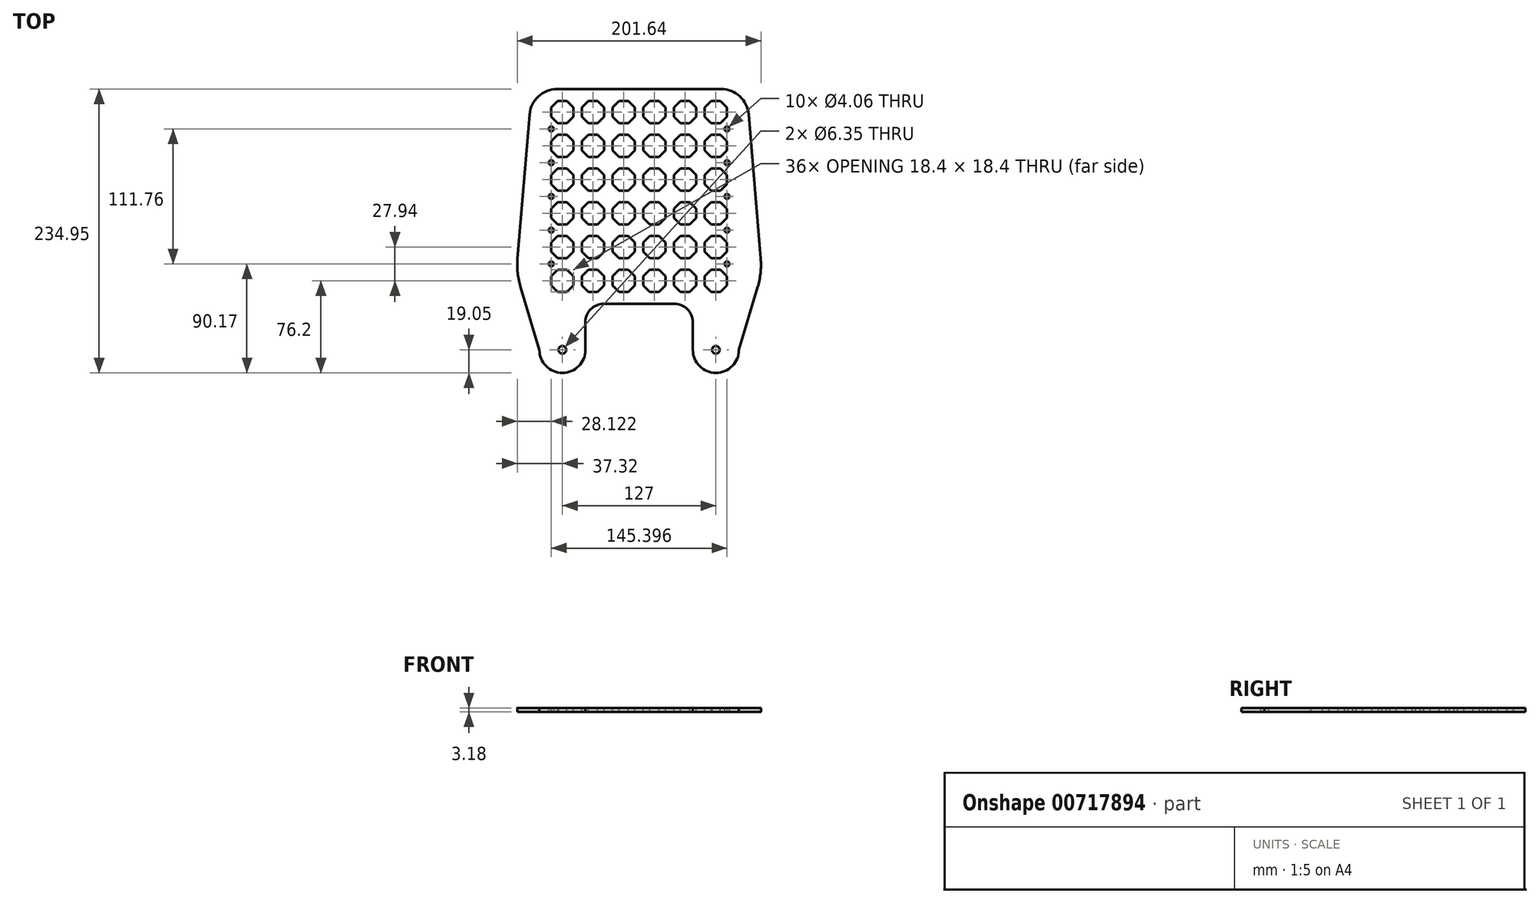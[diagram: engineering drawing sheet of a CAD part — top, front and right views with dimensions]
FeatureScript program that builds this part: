
annotation { "Feature Type Name" : "Feature", "Feature Type Description" : "" }
export const myFeature = defineFeature(function(context is Context, id is Id, definition is map)
    precondition{}
    {
        {
            var Q0;
            Q0=qCreatedBy(makeId("Top.planeOp"),FACE);
            var sketch = newSketch(context, id + "F0", { "sketchPlane" : qUnion([Q0])});
            skLineSegment(sketch, "E0.bottom", {"start": v(-67.87, 152.4) * mm, "end": v(67.87, 152.4) * mm});
            skPoint(sketch, "E0.middle", {"position": v(0, 0) * mm});
            skLineSegment(sketch, "E1", {"start": v(-101.6, 0) * mm, "end": v(101.6, 0) * mm});
            skLineSegment(sketch, "E2", {"start": v(0, 152.4) * mm, "end": v(0, 0) * mm, "construction": true});
            skLineSegment(sketch, "E3", {"start": v(-90.65, 131.44) * mm, "end": v(-100.6, 12) * mm});
            skLineSegment(sketch, "E4", {"start": v(90.65, 131.44) * mm, "end": v(100.6, 12) * mm});
            skLineSegment(sketch, "E5.top", {"start": v(-29.21, -25.4) * mm, "end": v(29.2, -25.4) * mm});
            skLineSegment(sketch, "E5.left", {"start": v(-101.6, 0) * mm, "end": v(-101.6, -25.4) * mm});
            skLineSegment(sketch, "E5.right", {"start": v(101.6, 0) * mm, "end": v(101.6, -25.4) * mm});
            skLineSegment(sketch, "E6.bottom", {"start": v(-82.55, -25.4) * mm, "end": v(-44.45, -25.4) * mm});
            skLineSegment(sketch, "E6.top", {"start": v(-82.55, -63.5) * mm, "end": v(-44.45, -63.5) * mm});
            skLineSegment(sketch, "E6.left", {"start": v(-82.55, -25.4) * mm, "end": v(-82.55, -63.5) * mm});
            skLineSegment(sketch, "E6.right", {"start": v(-44.45, -40.64) * mm, "end": v(-44.45, -63.5) * mm});
            skLineSegment(sketch, "E7.bottom", {"start": v(44.45, -25.4) * mm, "end": v(82.55, -25.4) * mm});
            skLineSegment(sketch, "E7.top", {"start": v(44.45, -63.5) * mm, "end": v(82.55, -63.5) * mm});
            skLineSegment(sketch, "E7.left", {"start": v(44.45, -40.64) * mm, "end": v(44.45, -63.5) * mm});
            skLineSegment(sketch, "E7.right", {"start": v(82.55, -25.4) * mm, "end": v(82.55, -63.5) * mm});
            skCircle(sketch, "E8", {"center": v(-63.5, -63.5) * mm, "radius": 19.05 * mm});
            skCircle(sketch, "E9", {"center": v(63.5, -63.5) * mm, "radius": 19.05 * mm});
            skLineSegment(sketch, "E10", {"start": v(-98.14, -11.53) * mm, "end": v(-82.55, -63.5) * mm});
            skLineSegment(sketch, "E11", {"start": v(98.14, -11.53) * mm, "end": v(82.55, -63.5) * mm});
            skPoint(sketch, "E12.visualSharp", {"position": v(-88.9, 152.4) * mm});
            skArc(sketch, "E12.filletArc", {"start": v(-67.87, 152.4) * mm, "mid": v(-83.34, 146.36) * mm, "end": v(-90.65, 131.44) * mm});
            skPoint(sketch, "E13.visualSharp", {"position": v(88.9, 152.4) * mm});
            skArc(sketch, "E13.filletArc", {"start": v(90.65, 131.44) * mm, "mid": v(83.34, 146.36) * mm, "end": v(67.87, 152.4) * mm});
            skPoint(sketch, "E14.visualSharp", {"position": v(101.6, 0) * mm});
            skArc(sketch, "E14.filletArc", {"start": v(98.14, -11.53) * mm, "mid": v(100.48, 0.12) * mm, "end": v(100.6, 12) * mm});
            skPoint(sketch, "E15.visualSharp", {"position": v(-101.6, 0) * mm});
            skArc(sketch, "E15.filletArc", {"start": v(-100.6, 12) * mm, "mid": v(-100.48, 0.12) * mm, "end": v(-98.14, -11.53) * mm});
            skPoint(sketch, "E16.newPointB", {"position": v(-101.6, -25.4) * mm});
            skArc(sketch, "E16.filletArc", {"start": v(-29.21, -25.4) * mm, "mid": v(-39.99, -29.86) * mm, "end": v(-44.45, -40.64) * mm});
            skPoint(sketch, "E17.newPointB", {"position": v(101.6, -25.4) * mm});
            skArc(sketch, "E17.filletArc", {"start": v(44.45, -40.64) * mm, "mid": v(39.99, -29.86) * mm, "end": v(29.2, -25.4) * mm});
            skCircle(sketch, "E18", {"center": v(-63.5, -63.5) * mm, "radius": 3.18 * mm});
            skCircle(sketch, "E19", {"center": v(63.5, -63.5) * mm, "radius": 3.18 * mm});
            skSolve(sketch);
        }
        {
            var Q0;
            Q0=makeQuery(id+"F0.imprint","IMPRINT",FACE,{"disambiguationData":[TD([[makeQuery(id+"F0.imprint","IMPRINT",EDGE,{"derivedFrom":sQuery(id+"F0.wireOp",EDGE,"E0.bottom")}),-1.0]])]});
            var Q1;
            {var subQ7=sQuery(id+"F0.wireOp",EDGE,"E1");Q1=makeQuery(id+"F0.imprint","IMPRINT",FACE,{"disambiguationData":[TD([[makeQuery(id+"F0.imprint","IMPRINT",EDGE,{"derivedFrom":subQ7}),-1.0]])]});}
            var Q2;
            Q2=makeQuery(id+"F0.imprint","IMPRINT",FACE,{"disambiguationData":[TD([[makeQuery(id+"F0.imprint","IMPRINT",EDGE,{"derivedFrom":sQuery(id+"F0.wireOp",EDGE,"E6.bottom")}),-1.0]])]});
            var Q3;
            {var subQ0=sQuery(id+"F0.wireOp",EDGE,"E6.left");Q3=makeQuery(id+"F0.imprint","IMPRINT",FACE,{"disambiguationData":[TD([[makeQuery(id+"F0.imprint","IMPRINT",EDGE,{"derivedFrom":subQ0}),-1.0]])]});}
            var Q4;
            {var subQ0=sQuery(id+"F0.wireOp",EDGE,"E6.top");Q4=makeQuery(id+"F0.imprint","IMPRINT",FACE,{"disambiguationData":[TD([[makeQuery(id+"F0.imprint","IMPRINT",EDGE,{"derivedFrom":subQ0}),1.0]])]});}
            var Q5;
            {var subQ0=sQuery(id+"F0.wireOp",EDGE,"E6.top");Q5=makeQuery(id+"F0.imprint","IMPRINT",FACE,{"disambiguationData":[TD([[makeQuery(id+"F0.imprint","IMPRINT",EDGE,{"derivedFrom":subQ0}),-1.0]])]});}
            var Q6;
            {var subQ0=sQuery(id+"F0.wireOp",EDGE,"E7.top");Q6=makeQuery(id+"F0.imprint","IMPRINT",FACE,{"disambiguationData":[TD([[makeQuery(id+"F0.imprint","IMPRINT",EDGE,{"derivedFrom":subQ0}),-1.0]])]});}
            var Q7;
            {var subQ0=sQuery(id+"F0.wireOp",EDGE,"E7.top");Q7=makeQuery(id+"F0.imprint","IMPRINT",FACE,{"disambiguationData":[TD([[makeQuery(id+"F0.imprint","IMPRINT",EDGE,{"derivedFrom":subQ0}),1.0]])]});}
            var Q8;
            Q8=makeQuery(id+"F0.imprint","IMPRINT",FACE,{"disambiguationData":[TD([[makeQuery(id+"F0.imprint","IMPRINT",EDGE,{"derivedFrom":sQuery(id+"F0.wireOp",EDGE,"E7.bottom")}),-1.0]])]});
            var Q9;
            {var subQ0=sQuery(id+"F0.wireOp",EDGE,"E7.right");Q9=makeQuery(id+"F0.imprint","IMPRINT",FACE,{"disambiguationData":[TD([[makeQuery(id+"F0.imprint","IMPRINT",EDGE,{"derivedFrom":subQ0}),1.0]])]});}
            extrude(context, id + "F1", {"entities" : qUnion([Q0, Q1, Q2, Q3, Q4, Q5, Q6, Q7, Q8, Q9]), "depth" : 3.17 * mm, "offsetDistance" : 25.4 * mm});
        }
        {
            var Q0;
            Q0=makeQuery(id+"F1.opExtrude","CAP_FACE",FACE,{"disambiguationData":[OSD([sQuery(id+"F0.wireOp",EDGE,"E0.bottom"),sQuery(id+"F0.wireOp",EDGE,"E3"),sQuery(id+"F0.wireOp",EDGE,"E4"),sQuery(id+"F0.wireOp",EDGE,"E5.top"),sQuery(id+"F0.wireOp",EDGE,"E6.right"),sQuery(id+"F0.wireOp",EDGE,"E7.left"),sQuery(id+"F0.wireOp",EDGE,"E8"),sQuery(id+"F0.wireOp",EDGE,"E9"),sQuery(id+"F0.wireOp",EDGE,"E10"),sQuery(id+"F0.wireOp",EDGE,"E11"),sQuery(id+"F0.wireOp",EDGE,"E12.filletArc"),sQuery(id+"F0.wireOp",EDGE,"E13.filletArc"),sQuery(id+"F0.wireOp",EDGE,"E14.filletArc"),sQuery(id+"F0.wireOp",EDGE,"E15.filletArc"),sQuery(id+"F0.wireOp",EDGE,"E16.filletArc"),sQuery(id+"F0.wireOp",EDGE,"E17.filletArc"),sQuery(id+"F0.wireOp",EDGE,"E18"),sQuery(id+"F0.wireOp",EDGE,"E19")])],"isStart":false});
            var sketch = newSketch(context, id + "F2", { "sketchPlane" : qUnion([Q0])});
            skCircle(sketch, "E20.cCircle", {"center": v(-63.5, 133.35) * mm, "radius": 9.2 * mm, "construction": true});
            skLineSegment(sketch, "E20.0", {"start": v(-54.3, 129.54) * mm, "end": v(-59.7, 124.15) * mm});
            skLineSegment(sketch, "E20.1", {"start": v(-59.69, 124.15) * mm, "end": v(-67.3, 124.15) * mm});
            skLineSegment(sketch, "E20.2", {"start": v(-67.3, 124.15) * mm, "end": v(-72.7, 129.54) * mm});
            skLineSegment(sketch, "E20.3", {"start": v(-72.7, 129.54) * mm, "end": v(-72.7, 137.16) * mm});
            skLineSegment(sketch, "E20.4", {"start": v(-72.7, 137.16) * mm, "end": v(-67.31, 142.55) * mm});
            skLineSegment(sketch, "E20.5", {"start": v(-67.31, 142.55) * mm, "end": v(-59.7, 142.55) * mm});
            skLineSegment(sketch, "E20.6", {"start": v(-59.7, 142.55) * mm, "end": v(-54.3, 137.16) * mm});
            skLineSegment(sketch, "E20.7", {"start": v(-54.3, 137.16) * mm, "end": v(-54.3, 129.54) * mm});
            skPoint(sketch, "E20.0.midPoint", {"position": v(-57, 126.85) * mm});
            skLineSegment(sketch, "E21", {"start": v(0, 0) * mm, "end": v(0, 152.4) * mm, "construction": true});
            skLineSegment(sketch, "E22.0.1.0", {"start": v(-67.3, 96.21) * mm, "end": v(-72.7, 101.6) * mm});
            skLineSegment(sketch, "E22.0.1.1", {"start": v(-72.7, 101.6) * mm, "end": v(-72.7, 109.22) * mm});
            skLineSegment(sketch, "E22.0.1.2", {"start": v(-72.7, 109.22) * mm, "end": v(-67.31, 114.6) * mm});
            skLineSegment(sketch, "E22.0.1.3", {"start": v(-67.31, 114.6) * mm, "end": v(-59.7, 114.6) * mm});
            skLineSegment(sketch, "E22.0.1.4", {"start": v(-59.7, 114.6) * mm, "end": v(-54.3, 109.22) * mm});
            skLineSegment(sketch, "E22.0.1.5", {"start": v(-54.3, 109.22) * mm, "end": v(-54.3, 101.6) * mm});
            skLineSegment(sketch, "E22.0.1.6", {"start": v(-54.3, 101.6) * mm, "end": v(-59.69, 96.21) * mm});
            skLineSegment(sketch, "E22.0.1.7", {"start": v(-59.69, 96.21) * mm, "end": v(-67.3, 96.21) * mm});
            skLineSegment(sketch, "E22.0.2.0", {"start": v(-67.3, 68.27) * mm, "end": v(-72.7, 73.66) * mm});
            skLineSegment(sketch, "E22.0.2.1", {"start": v(-72.7, 73.66) * mm, "end": v(-72.7, 81.28) * mm});
            skLineSegment(sketch, "E22.0.2.2", {"start": v(-72.7, 81.28) * mm, "end": v(-67.31, 86.67) * mm});
            skLineSegment(sketch, "E22.0.2.3", {"start": v(-67.3, 86.67) * mm, "end": v(-59.7, 86.67) * mm});
            skLineSegment(sketch, "E22.0.2.4", {"start": v(-59.7, 86.67) * mm, "end": v(-54.3, 81.28) * mm});
            skLineSegment(sketch, "E22.0.2.5", {"start": v(-54.3, 81.28) * mm, "end": v(-54.3, 73.66) * mm});
            skLineSegment(sketch, "E22.0.2.6", {"start": v(-54.3, 73.66) * mm, "end": v(-59.69, 68.27) * mm});
            skLineSegment(sketch, "E22.0.2.7", {"start": v(-59.69, 68.27) * mm, "end": v(-67.3, 68.27) * mm});
            skLineSegment(sketch, "E22.0.3.0", {"start": v(-67.3, 40.33) * mm, "end": v(-72.7, 45.72) * mm});
            skLineSegment(sketch, "E22.0.3.1", {"start": v(-72.7, 45.72) * mm, "end": v(-72.7, 53.34) * mm});
            skLineSegment(sketch, "E22.0.3.2", {"start": v(-72.7, 53.34) * mm, "end": v(-67.3, 58.73) * mm});
            skLineSegment(sketch, "E22.0.3.3", {"start": v(-67.3, 58.73) * mm, "end": v(-59.69, 58.73) * mm});
            skLineSegment(sketch, "E22.0.3.4", {"start": v(-59.69, 58.73) * mm, "end": v(-54.3, 53.34) * mm});
            skLineSegment(sketch, "E22.0.3.5", {"start": v(-54.3, 53.34) * mm, "end": v(-54.3, 45.72) * mm});
            skLineSegment(sketch, "E22.0.3.6", {"start": v(-54.3, 45.72) * mm, "end": v(-59.69, 40.33) * mm});
            skLineSegment(sketch, "E22.0.3.7", {"start": v(-59.69, 40.33) * mm, "end": v(-67.3, 40.33) * mm});
            skLineSegment(sketch, "E22.0.4.0", {"start": v(-67.3, 12.4) * mm, "end": v(-72.7, 17.78) * mm});
            skLineSegment(sketch, "E22.0.4.1", {"start": v(-72.7, 17.78) * mm, "end": v(-72.7, 25.4) * mm});
            skLineSegment(sketch, "E22.0.4.2", {"start": v(-72.7, 25.4) * mm, "end": v(-67.3, 30.79) * mm});
            skLineSegment(sketch, "E22.0.4.3", {"start": v(-67.3, 30.79) * mm, "end": v(-59.69, 30.79) * mm});
            skLineSegment(sketch, "E22.0.4.4", {"start": v(-59.69, 30.79) * mm, "end": v(-54.3, 25.4) * mm});
            skLineSegment(sketch, "E22.0.4.5", {"start": v(-54.3, 25.4) * mm, "end": v(-54.3, 17.78) * mm});
            skLineSegment(sketch, "E22.0.4.6", {"start": v(-54.3, 17.78) * mm, "end": v(-59.69, 12.4) * mm});
            skLineSegment(sketch, "E22.0.4.7", {"start": v(-59.69, 12.4) * mm, "end": v(-67.3, 12.4) * mm});
            skLineSegment(sketch, "E22.0.5.0", {"start": v(-67.3, -15.55) * mm, "end": v(-72.7, -10.16) * mm});
            skLineSegment(sketch, "E22.0.5.1", {"start": v(-72.7, -10.16) * mm, "end": v(-72.7, -2.54) * mm});
            skLineSegment(sketch, "E22.0.5.2", {"start": v(-72.7, -2.54) * mm, "end": v(-67.3, 2.85) * mm});
            skLineSegment(sketch, "E22.0.5.3", {"start": v(-67.3, 2.85) * mm, "end": v(-59.69, 2.85) * mm});
            skLineSegment(sketch, "E22.0.5.4", {"start": v(-59.69, 2.85) * mm, "end": v(-54.3, -2.54) * mm});
            skLineSegment(sketch, "E22.0.5.5", {"start": v(-54.3, -2.54) * mm, "end": v(-54.3, -10.16) * mm});
            skLineSegment(sketch, "E22.0.5.6", {"start": v(-54.3, -10.16) * mm, "end": v(-59.69, -15.55) * mm});
            skLineSegment(sketch, "E22.0.5.7", {"start": v(-59.69, -15.55) * mm, "end": v(-67.3, -15.55) * mm});
            skLineSegment(sketch, "E22.1.0.0", {"start": v(-41.91, 124.15) * mm, "end": v(-47.3, 129.54) * mm});
            skLineSegment(sketch, "E22.1.0.1", {"start": v(-47.3, 129.54) * mm, "end": v(-47.3, 137.16) * mm});
            skLineSegment(sketch, "E22.1.0.2", {"start": v(-47.3, 137.16) * mm, "end": v(-41.91, 142.55) * mm});
            skLineSegment(sketch, "E22.1.0.3", {"start": v(-41.91, 142.55) * mm, "end": v(-34.3, 142.55) * mm});
            skLineSegment(sketch, "E22.1.0.4", {"start": v(-34.3, 142.55) * mm, "end": v(-28.9, 137.16) * mm});
            skLineSegment(sketch, "E22.1.0.5", {"start": v(-28.9, 137.16) * mm, "end": v(-28.9, 129.54) * mm});
            skLineSegment(sketch, "E22.1.0.6", {"start": v(-28.9, 129.54) * mm, "end": v(-34.3, 124.15) * mm});
            skLineSegment(sketch, "E22.1.0.7", {"start": v(-34.29, 124.15) * mm, "end": v(-41.9, 124.15) * mm});
            skLineSegment(sketch, "E22.1.1.0", {"start": v(-41.9, 96.21) * mm, "end": v(-47.3, 101.6) * mm});
            skLineSegment(sketch, "E22.1.1.1", {"start": v(-47.3, 101.6) * mm, "end": v(-47.3, 109.22) * mm});
            skLineSegment(sketch, "E22.1.1.2", {"start": v(-47.3, 109.22) * mm, "end": v(-41.91, 114.6) * mm});
            skLineSegment(sketch, "E22.1.1.3", {"start": v(-41.91, 114.6) * mm, "end": v(-34.3, 114.6) * mm});
            skLineSegment(sketch, "E22.1.1.4", {"start": v(-34.3, 114.6) * mm, "end": v(-28.9, 109.22) * mm});
            skLineSegment(sketch, "E22.1.1.5", {"start": v(-28.9, 109.22) * mm, "end": v(-28.9, 101.6) * mm});
            skLineSegment(sketch, "E22.1.1.6", {"start": v(-28.9, 101.6) * mm, "end": v(-34.3, 96.21) * mm});
            skLineSegment(sketch, "E22.1.1.7", {"start": v(-34.29, 96.21) * mm, "end": v(-41.9, 96.21) * mm});
            skLineSegment(sketch, "E22.1.2.0", {"start": v(-41.9, 68.27) * mm, "end": v(-47.3, 73.66) * mm});
            skLineSegment(sketch, "E22.1.2.1", {"start": v(-47.3, 73.66) * mm, "end": v(-47.3, 81.28) * mm});
            skLineSegment(sketch, "E22.1.2.2", {"start": v(-47.3, 81.28) * mm, "end": v(-41.91, 86.67) * mm});
            skLineSegment(sketch, "E22.1.2.3", {"start": v(-41.91, 86.67) * mm, "end": v(-34.3, 86.67) * mm});
            skLineSegment(sketch, "E22.1.2.4", {"start": v(-34.3, 86.67) * mm, "end": v(-28.9, 81.28) * mm});
            skLineSegment(sketch, "E22.1.2.5", {"start": v(-28.9, 81.28) * mm, "end": v(-28.9, 73.66) * mm});
            skLineSegment(sketch, "E22.1.2.6", {"start": v(-28.9, 73.66) * mm, "end": v(-34.29, 68.27) * mm});
            skLineSegment(sketch, "E22.1.2.7", {"start": v(-34.29, 68.27) * mm, "end": v(-41.9, 68.27) * mm});
            skLineSegment(sketch, "E22.1.3.0", {"start": v(-41.9, 40.33) * mm, "end": v(-47.3, 45.72) * mm});
            skLineSegment(sketch, "E22.1.3.1", {"start": v(-47.3, 45.72) * mm, "end": v(-47.3, 53.34) * mm});
            skLineSegment(sketch, "E22.1.3.2", {"start": v(-47.3, 53.34) * mm, "end": v(-41.91, 58.73) * mm});
            skLineSegment(sketch, "E22.1.3.3", {"start": v(-41.9, 58.73) * mm, "end": v(-34.3, 58.73) * mm});
            skLineSegment(sketch, "E22.1.3.4", {"start": v(-34.3, 58.73) * mm, "end": v(-28.9, 53.34) * mm});
            skLineSegment(sketch, "E22.1.3.5", {"start": v(-28.9, 53.34) * mm, "end": v(-28.9, 45.72) * mm});
            skLineSegment(sketch, "E22.1.3.6", {"start": v(-28.9, 45.72) * mm, "end": v(-34.29, 40.33) * mm});
            skLineSegment(sketch, "E22.1.3.7", {"start": v(-34.29, 40.33) * mm, "end": v(-41.91, 40.33) * mm});
            skLineSegment(sketch, "E22.1.4.0", {"start": v(-41.91, 12.4) * mm, "end": v(-47.3, 17.78) * mm});
            skLineSegment(sketch, "E22.1.4.1", {"start": v(-47.3, 17.78) * mm, "end": v(-47.3, 25.4) * mm});
            skLineSegment(sketch, "E22.1.4.2", {"start": v(-47.3, 25.4) * mm, "end": v(-41.91, 30.79) * mm});
            skLineSegment(sketch, "E22.1.4.3", {"start": v(-41.9, 30.79) * mm, "end": v(-34.29, 30.79) * mm});
            skLineSegment(sketch, "E22.1.4.4", {"start": v(-34.29, 30.79) * mm, "end": v(-28.9, 25.4) * mm});
            skLineSegment(sketch, "E22.1.4.5", {"start": v(-28.9, 25.4) * mm, "end": v(-28.9, 17.78) * mm});
            skLineSegment(sketch, "E22.1.4.6", {"start": v(-28.9, 17.78) * mm, "end": v(-34.29, 12.4) * mm});
            skLineSegment(sketch, "E22.1.4.7", {"start": v(-34.29, 12.4) * mm, "end": v(-41.91, 12.4) * mm});
            skLineSegment(sketch, "E22.1.5.0", {"start": v(-41.91, -15.55) * mm, "end": v(-47.3, -10.16) * mm});
            skLineSegment(sketch, "E22.1.5.1", {"start": v(-47.3, -10.16) * mm, "end": v(-47.3, -2.54) * mm});
            skLineSegment(sketch, "E22.1.5.2", {"start": v(-47.3, -2.54) * mm, "end": v(-41.9, 2.85) * mm});
            skLineSegment(sketch, "E22.1.5.3", {"start": v(-41.9, 2.85) * mm, "end": v(-34.29, 2.85) * mm});
            skLineSegment(sketch, "E22.1.5.4", {"start": v(-34.29, 2.85) * mm, "end": v(-28.9, -2.54) * mm});
            skLineSegment(sketch, "E22.1.5.5", {"start": v(-28.9, -2.54) * mm, "end": v(-28.9, -10.16) * mm});
            skLineSegment(sketch, "E22.1.5.6", {"start": v(-28.9, -10.16) * mm, "end": v(-34.29, -15.55) * mm});
            skLineSegment(sketch, "E22.1.5.7", {"start": v(-34.29, -15.55) * mm, "end": v(-41.91, -15.55) * mm});
            skLineSegment(sketch, "E22.2.0.0", {"start": v(-16.51, 124.15) * mm, "end": v(-21.9, 129.54) * mm});
            skLineSegment(sketch, "E22.2.0.1", {"start": v(-21.9, 129.54) * mm, "end": v(-21.9, 137.16) * mm});
            skLineSegment(sketch, "E22.2.0.2", {"start": v(-21.9, 137.16) * mm, "end": v(-16.51, 142.55) * mm});
            skLineSegment(sketch, "E22.2.0.3", {"start": v(-16.51, 142.55) * mm, "end": v(-8.9, 142.55) * mm});
            skLineSegment(sketch, "E22.2.0.4", {"start": v(-8.9, 142.55) * mm, "end": v(-3.5, 137.16) * mm});
            skLineSegment(sketch, "E22.2.0.5", {"start": v(-3.5, 137.16) * mm, "end": v(-3.5, 129.54) * mm});
            skLineSegment(sketch, "E22.2.0.6", {"start": v(-3.5, 129.54) * mm, "end": v(-8.9, 124.15) * mm});
            skLineSegment(sketch, "E22.2.0.7", {"start": v(-8.89, 124.15) * mm, "end": v(-16.5, 124.15) * mm});
            skLineSegment(sketch, "E22.2.1.0", {"start": v(-16.51, 96.21) * mm, "end": v(-21.9, 101.6) * mm});
            skLineSegment(sketch, "E22.2.1.1", {"start": v(-21.9, 101.6) * mm, "end": v(-21.9, 109.22) * mm});
            skLineSegment(sketch, "E22.2.1.2", {"start": v(-21.9, 109.22) * mm, "end": v(-16.51, 114.6) * mm});
            skLineSegment(sketch, "E22.2.1.3", {"start": v(-16.51, 114.6) * mm, "end": v(-8.9, 114.6) * mm});
            skLineSegment(sketch, "E22.2.1.4", {"start": v(-8.9, 114.6) * mm, "end": v(-3.5, 109.22) * mm});
            skLineSegment(sketch, "E22.2.1.5", {"start": v(-3.5, 109.22) * mm, "end": v(-3.5, 101.6) * mm});
            skLineSegment(sketch, "E22.2.1.6", {"start": v(-3.5, 101.6) * mm, "end": v(-8.9, 96.21) * mm});
            skLineSegment(sketch, "E22.2.1.7", {"start": v(-8.89, 96.21) * mm, "end": v(-16.5, 96.21) * mm});
            skLineSegment(sketch, "E22.2.2.0", {"start": v(-16.5, 68.27) * mm, "end": v(-21.9, 73.66) * mm});
            skLineSegment(sketch, "E22.2.2.1", {"start": v(-21.9, 73.66) * mm, "end": v(-21.9, 81.28) * mm});
            skLineSegment(sketch, "E22.2.2.2", {"start": v(-21.9, 81.28) * mm, "end": v(-16.51, 86.67) * mm});
            skLineSegment(sketch, "E22.2.2.3", {"start": v(-16.51, 86.67) * mm, "end": v(-8.9, 86.67) * mm});
            skLineSegment(sketch, "E22.2.2.4", {"start": v(-8.9, 86.67) * mm, "end": v(-3.5, 81.28) * mm});
            skLineSegment(sketch, "E22.2.2.5", {"start": v(-3.5, 81.28) * mm, "end": v(-3.5, 73.66) * mm});
            skLineSegment(sketch, "E22.2.2.6", {"start": v(-3.5, 73.66) * mm, "end": v(-8.9, 68.27) * mm});
            skLineSegment(sketch, "E22.2.2.7", {"start": v(-8.89, 68.27) * mm, "end": v(-16.5, 68.27) * mm});
            skLineSegment(sketch, "E22.2.3.0", {"start": v(-16.5, 40.33) * mm, "end": v(-21.9, 45.72) * mm});
            skLineSegment(sketch, "E22.2.3.1", {"start": v(-21.9, 45.72) * mm, "end": v(-21.9, 53.34) * mm});
            skLineSegment(sketch, "E22.2.3.2", {"start": v(-21.9, 53.34) * mm, "end": v(-16.51, 58.73) * mm});
            skLineSegment(sketch, "E22.2.3.3", {"start": v(-16.5, 58.73) * mm, "end": v(-8.9, 58.73) * mm});
            skLineSegment(sketch, "E22.2.3.4", {"start": v(-8.9, 58.73) * mm, "end": v(-3.5, 53.34) * mm});
            skLineSegment(sketch, "E22.2.3.5", {"start": v(-3.5, 53.34) * mm, "end": v(-3.5, 45.72) * mm});
            skLineSegment(sketch, "E22.2.3.6", {"start": v(-3.5, 45.72) * mm, "end": v(-8.89, 40.33) * mm});
            skLineSegment(sketch, "E22.2.3.7", {"start": v(-8.89, 40.33) * mm, "end": v(-16.5, 40.33) * mm});
            skLineSegment(sketch, "E22.2.4.0", {"start": v(-16.5, 12.4) * mm, "end": v(-21.9, 17.78) * mm});
            skLineSegment(sketch, "E22.2.4.1", {"start": v(-21.9, 17.78) * mm, "end": v(-21.9, 25.4) * mm});
            skLineSegment(sketch, "E22.2.4.2", {"start": v(-21.9, 25.4) * mm, "end": v(-16.51, 30.79) * mm});
            skLineSegment(sketch, "E22.2.4.3", {"start": v(-16.5, 30.79) * mm, "end": v(-8.89, 30.79) * mm});
            skLineSegment(sketch, "E22.2.4.4", {"start": v(-8.9, 30.79) * mm, "end": v(-3.5, 25.4) * mm});
            skLineSegment(sketch, "E22.2.4.5", {"start": v(-3.5, 25.4) * mm, "end": v(-3.5, 17.78) * mm});
            skLineSegment(sketch, "E22.2.4.6", {"start": v(-3.5, 17.78) * mm, "end": v(-8.89, 12.4) * mm});
            skLineSegment(sketch, "E22.2.4.7", {"start": v(-8.89, 12.4) * mm, "end": v(-16.5, 12.4) * mm});
            skLineSegment(sketch, "E22.2.5.0", {"start": v(-16.5, -15.55) * mm, "end": v(-21.9, -10.16) * mm});
            skLineSegment(sketch, "E22.2.5.1", {"start": v(-21.9, -10.16) * mm, "end": v(-21.9, -2.54) * mm});
            skLineSegment(sketch, "E22.2.5.2", {"start": v(-21.9, -2.54) * mm, "end": v(-16.51, 2.85) * mm});
            skLineSegment(sketch, "E22.2.5.3", {"start": v(-16.5, 2.85) * mm, "end": v(-8.89, 2.85) * mm});
            skLineSegment(sketch, "E22.2.5.4", {"start": v(-8.89, 2.85) * mm, "end": v(-3.5, -2.54) * mm});
            skLineSegment(sketch, "E22.2.5.5", {"start": v(-3.5, -2.54) * mm, "end": v(-3.5, -10.16) * mm});
            skLineSegment(sketch, "E22.2.5.6", {"start": v(-3.5, -10.16) * mm, "end": v(-8.89, -15.55) * mm});
            skLineSegment(sketch, "E22.2.5.7", {"start": v(-8.89, -15.55) * mm, "end": v(-16.5, -15.55) * mm});
            skLineSegment(sketch, "E22.direction1", {"start": v(-67.3, 124.15) * mm, "end": v(-41.9, 124.15) * mm, "construction": true});
            skLineSegment(sketch, "E22.direction2", {"start": v(-67.3, 124.15) * mm, "end": v(-67.3, 96.21) * mm, "construction": true});
            skLineSegment(sketch, "E23.MirrorCS", {"start": v(67.31, 142.55) * mm, "end": v(59.7, 142.55) * mm});
            skLineSegment(sketch, "E24.MirrorCS", {"start": v(59.7, 142.55) * mm, "end": v(54.3, 137.16) * mm});
            skLineSegment(sketch, "E25.MirrorCS", {"start": v(54.3, 137.16) * mm, "end": v(54.3, 129.54) * mm});
            skLineSegment(sketch, "E26.MirrorCS", {"start": v(67.3, 96.21) * mm, "end": v(72.7, 101.6) * mm});
            skLineSegment(sketch, "E27.MirrorCS", {"start": v(72.7, 109.22) * mm, "end": v(67.31, 114.6) * mm});
            skLineSegment(sketch, "E28.MirrorCS", {"start": v(72.7, 137.16) * mm, "end": v(67.31, 142.55) * mm});
            skLineSegment(sketch, "E29.MirrorCS", {"start": v(72.7, 129.54) * mm, "end": v(72.7, 137.16) * mm});
            skLineSegment(sketch, "E30.MirrorCS", {"start": v(59.69, 124.15) * mm, "end": v(67.3, 124.15) * mm});
            skLineSegment(sketch, "E31.MirrorCS", {"start": v(54.3, 129.54) * mm, "end": v(59.7, 124.15) * mm});
            skLineSegment(sketch, "E32.MirrorCS", {"start": v(59.7, 114.6) * mm, "end": v(54.3, 109.22) * mm});
            skLineSegment(sketch, "E33.MirrorCS", {"start": v(67.31, 114.6) * mm, "end": v(59.7, 114.6) * mm});
            skLineSegment(sketch, "E34.MirrorCS", {"start": v(34.29, 124.15) * mm, "end": v(41.9, 124.15) * mm});
            skLineSegment(sketch, "E35.MirrorCS", {"start": v(72.7, 101.6) * mm, "end": v(72.7, 109.22) * mm});
            skLineSegment(sketch, "E36.MirrorCS", {"start": v(67.3, 58.73) * mm, "end": v(59.69, 58.73) * mm});
            skLineSegment(sketch, "E37.MirrorCS", {"start": v(41.9, 2.85) * mm, "end": v(34.29, 2.85) * mm});
            skLineSegment(sketch, "E38.MirrorCS", {"start": v(41.9, 58.73) * mm, "end": v(34.3, 58.73) * mm});
            skLineSegment(sketch, "E39.MirrorCS", {"start": v(41.91, 114.6) * mm, "end": v(34.3, 114.6) * mm});
            skLineSegment(sketch, "E40.MirrorCS", {"start": v(67.3, 2.85) * mm, "end": v(59.69, 2.85) * mm});
            skLineSegment(sketch, "E41.MirrorCS", {"start": v(16.5, 2.85) * mm, "end": v(8.89, 2.85) * mm});
            skLineSegment(sketch, "E42.MirrorCS", {"start": v(16.5, 58.73) * mm, "end": v(8.9, 58.73) * mm});
            skLineSegment(sketch, "E43.MirrorCS", {"start": v(16.51, 114.6) * mm, "end": v(8.9, 114.6) * mm});
            skLineSegment(sketch, "E44.MirrorCS", {"start": v(59.69, 58.73) * mm, "end": v(54.3, 53.34) * mm});
            skLineSegment(sketch, "E45.MirrorCS", {"start": v(34.29, 2.85) * mm, "end": v(28.9, -2.54) * mm});
            skLineSegment(sketch, "E46.MirrorCS", {"start": v(34.29, 58.73) * mm, "end": v(28.9, 53.34) * mm});
            skLineSegment(sketch, "E47.MirrorCS", {"start": v(34.3, 114.6) * mm, "end": v(28.9, 109.22) * mm});
            skLineSegment(sketch, "E48.MirrorCS", {"start": v(59.69, 2.85) * mm, "end": v(54.3, -2.54) * mm});
            skLineSegment(sketch, "E49.MirrorCS", {"start": v(8.89, 2.85) * mm, "end": v(3.5, -2.54) * mm});
            skLineSegment(sketch, "E50.MirrorCS", {"start": v(8.9, 58.73) * mm, "end": v(3.5, 53.34) * mm});
            skLineSegment(sketch, "E51.MirrorCS", {"start": v(8.9, 114.6) * mm, "end": v(3.5, 109.22) * mm});
            skLineSegment(sketch, "E52.MirrorCS", {"start": v(54.3, 53.34) * mm, "end": v(54.3, 45.72) * mm});
            skLineSegment(sketch, "E53.MirrorCS", {"start": v(28.9, -2.54) * mm, "end": v(28.9, -10.16) * mm});
            skLineSegment(sketch, "E54.MirrorCS", {"start": v(28.9, 53.34) * mm, "end": v(28.9, 45.72) * mm});
            skLineSegment(sketch, "E55.MirrorCS", {"start": v(28.9, 109.22) * mm, "end": v(28.9, 101.6) * mm});
            skLineSegment(sketch, "E56.MirrorCS", {"start": v(54.3, -2.54) * mm, "end": v(54.3, -10.16) * mm});
            skLineSegment(sketch, "E57.MirrorCS", {"start": v(3.5, -2.54) * mm, "end": v(3.5, -10.16) * mm});
            skLineSegment(sketch, "E58.MirrorCS", {"start": v(3.5, 53.34) * mm, "end": v(3.5, 45.72) * mm});
            skLineSegment(sketch, "E59.MirrorCS", {"start": v(3.5, 109.22) * mm, "end": v(3.5, 101.6) * mm});
            skLineSegment(sketch, "E60.MirrorCS", {"start": v(28.9, -10.16) * mm, "end": v(34.29, -15.55) * mm});
            skLineSegment(sketch, "E61.MirrorCS", {"start": v(28.9, 45.72) * mm, "end": v(34.29, 40.33) * mm});
            skLineSegment(sketch, "E62.MirrorCS", {"start": v(28.9, 101.6) * mm, "end": v(34.3, 96.21) * mm});
            skLineSegment(sketch, "E63.MirrorCS", {"start": v(54.3, -10.16) * mm, "end": v(59.69, -15.55) * mm});
            skLineSegment(sketch, "E64.MirrorCS", {"start": v(3.5, -10.16) * mm, "end": v(8.89, -15.55) * mm});
            skLineSegment(sketch, "E65.MirrorCS", {"start": v(3.5, 45.72) * mm, "end": v(8.89, 40.33) * mm});
            skLineSegment(sketch, "E66.MirrorCS", {"start": v(3.5, 101.6) * mm, "end": v(8.9, 96.21) * mm});
            skLineSegment(sketch, "E67.MirrorCS", {"start": v(54.3, 45.72) * mm, "end": v(59.69, 40.33) * mm});
            skLineSegment(sketch, "E68.MirrorCS", {"start": v(54.3, 101.6) * mm, "end": v(59.69, 96.21) * mm});
            skLineSegment(sketch, "E69.MirrorCS", {"start": v(8.89, -15.55) * mm, "end": v(16.5, -15.55) * mm});
            skLineSegment(sketch, "E70.MirrorCS", {"start": v(8.89, 40.33) * mm, "end": v(16.5, 40.33) * mm});
            skLineSegment(sketch, "E71.MirrorCS", {"start": v(8.89, 96.21) * mm, "end": v(16.5, 96.21) * mm});
            skLineSegment(sketch, "E72.MirrorCS", {"start": v(59.69, 40.33) * mm, "end": v(67.3, 40.33) * mm});
            skLineSegment(sketch, "E73.MirrorCS", {"start": v(59.69, 96.21) * mm, "end": v(67.3, 96.21) * mm});
            skLineSegment(sketch, "E74.MirrorCS", {"start": v(34.29, -15.55) * mm, "end": v(41.91, -15.55) * mm});
            skLineSegment(sketch, "E75.MirrorCS", {"start": v(34.29, 40.33) * mm, "end": v(41.91, 40.33) * mm});
            skLineSegment(sketch, "E76.MirrorCS", {"start": v(34.29, 96.21) * mm, "end": v(41.9, 96.21) * mm});
            skLineSegment(sketch, "E77.MirrorCS", {"start": v(59.69, -15.55) * mm, "end": v(67.3, -15.55) * mm});
            skLineSegment(sketch, "E78.MirrorCS", {"start": v(67.3, 12.4) * mm, "end": v(72.7, 17.78) * mm});
            skLineSegment(sketch, "E79.MirrorCS", {"start": v(67.3, 68.27) * mm, "end": v(72.7, 73.66) * mm});
            skLineSegment(sketch, "E80.MirrorCS", {"start": v(16.51, 124.15) * mm, "end": v(21.9, 129.54) * mm});
            skLineSegment(sketch, "E81.MirrorCS", {"start": v(41.91, 12.4) * mm, "end": v(47.3, 17.78) * mm});
            skLineSegment(sketch, "E82.MirrorCS", {"start": v(41.9, 68.27) * mm, "end": v(47.3, 73.66) * mm});
            skLineSegment(sketch, "E83.MirrorCS", {"start": v(41.9, 124.15) * mm, "end": v(47.3, 129.54) * mm});
            skLineSegment(sketch, "E84.MirrorCS", {"start": v(67.3, 124.15) * mm, "end": v(41.9, 124.15) * mm, "construction": true});
            skLineSegment(sketch, "E85.MirrorCS", {"start": v(16.5, 12.4) * mm, "end": v(21.9, 17.78) * mm});
            skLineSegment(sketch, "E86.MirrorCS", {"start": v(16.5, 68.27) * mm, "end": v(21.9, 73.66) * mm});
            skLineSegment(sketch, "E87.MirrorCS", {"start": v(72.7, 17.78) * mm, "end": v(72.7, 25.4) * mm});
            skLineSegment(sketch, "E88.MirrorCS", {"start": v(72.7, 73.66) * mm, "end": v(72.7, 81.28) * mm});
            skLineSegment(sketch, "E89.MirrorCS", {"start": v(21.9, 129.54) * mm, "end": v(21.9, 137.16) * mm});
            skLineSegment(sketch, "E90.MirrorCS", {"start": v(47.3, 17.78) * mm, "end": v(47.3, 25.4) * mm});
            skLineSegment(sketch, "E91.MirrorCS", {"start": v(47.3, 73.66) * mm, "end": v(47.3, 81.28) * mm});
            skLineSegment(sketch, "E92.MirrorCS", {"start": v(47.3, 129.54) * mm, "end": v(47.3, 137.16) * mm});
            skLineSegment(sketch, "E93.MirrorCS", {"start": v(67.3, 124.15) * mm, "end": v(67.3, 96.21) * mm, "construction": true});
            skLineSegment(sketch, "E94.MirrorCS", {"start": v(21.9, 17.78) * mm, "end": v(21.9, 25.4) * mm});
            skLineSegment(sketch, "E95.MirrorCS", {"start": v(21.9, 73.66) * mm, "end": v(21.9, 81.28) * mm});
            skLineSegment(sketch, "E96.MirrorCS", {"start": v(72.7, 25.4) * mm, "end": v(67.3, 30.79) * mm});
            skLineSegment(sketch, "E97.MirrorCS", {"start": v(72.7, 81.28) * mm, "end": v(67.31, 86.67) * mm});
            skLineSegment(sketch, "E98.MirrorCS", {"start": v(21.9, 137.16) * mm, "end": v(16.51, 142.55) * mm});
            skLineSegment(sketch, "E99.MirrorCS", {"start": v(47.3, 25.4) * mm, "end": v(41.9, 30.79) * mm});
            skLineSegment(sketch, "E100.MirrorCS", {"start": v(47.3, 81.28) * mm, "end": v(41.91, 86.67) * mm});
            skLineSegment(sketch, "E101.MirrorCS", {"start": v(47.3, 137.16) * mm, "end": v(41.91, 142.55) * mm});
            skLineSegment(sketch, "E102.MirrorCS", {"start": v(21.9, 25.4) * mm, "end": v(16.51, 30.79) * mm});
            skLineSegment(sketch, "E103.MirrorCS", {"start": v(67.3, 124.15) * mm, "end": v(72.7, 129.54) * mm});
            skLineSegment(sketch, "E104.MirrorCS", {"start": v(47.3, -10.16) * mm, "end": v(47.3, -2.54) * mm});
            skLineSegment(sketch, "E105.MirrorCS", {"start": v(21.9, 101.6) * mm, "end": v(21.9, 109.22) * mm});
            skLineSegment(sketch, "E106.MirrorCS", {"start": v(21.9, 45.72) * mm, "end": v(21.9, 53.34) * mm});
            skLineSegment(sketch, "E107.MirrorCS", {"start": v(21.9, -10.16) * mm, "end": v(21.9, -2.54) * mm});
            skLineSegment(sketch, "E108.MirrorCS", {"start": v(72.7, 45.72) * mm, "end": v(72.7, 53.34) * mm});
            skLineSegment(sketch, "E109.MirrorCS", {"start": v(72.7, -10.16) * mm, "end": v(72.7, -2.54) * mm});
            skLineSegment(sketch, "E110.MirrorCS", {"start": v(47.3, 101.6) * mm, "end": v(47.3, 109.22) * mm});
            skLineSegment(sketch, "E111.MirrorCS", {"start": v(47.3, 45.72) * mm, "end": v(47.3, 53.34) * mm});
            skCircle(sketch, "E112.MirrorC", {"center": v(63.5, 133.35) * mm, "radius": 9.2 * mm, "construction": true});
            skLineSegment(sketch, "E113.MirrorCS", {"start": v(54.3, 109.22) * mm, "end": v(54.3, 101.6) * mm});
            skLineSegment(sketch, "E114.MirrorCS", {"start": v(41.91, -15.55) * mm, "end": v(47.3, -10.16) * mm});
            skLineSegment(sketch, "E115.MirrorCS", {"start": v(16.5, 96.21) * mm, "end": v(21.9, 101.6) * mm});
            skLineSegment(sketch, "E116.MirrorCS", {"start": v(16.5, 40.33) * mm, "end": v(21.9, 45.72) * mm});
            skLineSegment(sketch, "E117.MirrorCS", {"start": v(16.5, -15.55) * mm, "end": v(21.9, -10.16) * mm});
            skLineSegment(sketch, "E118.MirrorCS", {"start": v(67.3, 40.33) * mm, "end": v(72.7, 45.72) * mm});
            skLineSegment(sketch, "E119.MirrorCS", {"start": v(67.3, -15.55) * mm, "end": v(72.7, -10.16) * mm});
            skLineSegment(sketch, "E120.MirrorCS", {"start": v(41.9, 96.21) * mm, "end": v(47.3, 101.6) * mm});
            skLineSegment(sketch, "E121.MirrorCS", {"start": v(41.9, 40.33) * mm, "end": v(47.3, 45.72) * mm});
            skLineSegment(sketch, "E122.MirrorCS", {"start": v(34.29, 12.4) * mm, "end": v(41.91, 12.4) * mm});
            skLineSegment(sketch, "E123.MirrorCS", {"start": v(8.89, 124.15) * mm, "end": v(16.5, 124.15) * mm});
            skLineSegment(sketch, "E124.MirrorCS", {"start": v(8.89, 68.27) * mm, "end": v(16.5, 68.27) * mm});
            skLineSegment(sketch, "E125.MirrorCS", {"start": v(8.89, 12.4) * mm, "end": v(16.5, 12.4) * mm});
            skLineSegment(sketch, "E126.MirrorCS", {"start": v(59.69, 68.27) * mm, "end": v(67.3, 68.27) * mm});
            skLineSegment(sketch, "E127.MirrorCS", {"start": v(59.69, 12.4) * mm, "end": v(67.3, 12.4) * mm});
            skLineSegment(sketch, "E128.MirrorCS", {"start": v(34.29, 68.27) * mm, "end": v(41.9, 68.27) * mm});
            skLineSegment(sketch, "E129.MirrorCS", {"start": v(28.9, 17.78) * mm, "end": v(34.29, 12.4) * mm});
            skLineSegment(sketch, "E130.MirrorCS", {"start": v(3.5, 129.54) * mm, "end": v(8.9, 124.15) * mm});
            skLineSegment(sketch, "E131.MirrorCS", {"start": v(3.5, 73.66) * mm, "end": v(8.9, 68.27) * mm});
            skLineSegment(sketch, "E132.MirrorCS", {"start": v(3.5, 17.78) * mm, "end": v(8.89, 12.4) * mm});
            skLineSegment(sketch, "E133.MirrorCS", {"start": v(54.3, 73.66) * mm, "end": v(59.69, 68.27) * mm});
            skLineSegment(sketch, "E134.MirrorCS", {"start": v(54.3, 17.78) * mm, "end": v(59.69, 12.4) * mm});
            skLineSegment(sketch, "E135.MirrorCS", {"start": v(28.9, 129.54) * mm, "end": v(34.3, 124.15) * mm});
            skLineSegment(sketch, "E136.MirrorCS", {"start": v(28.9, 73.66) * mm, "end": v(34.29, 68.27) * mm});
            skLineSegment(sketch, "E137.MirrorCS", {"start": v(28.9, 25.4) * mm, "end": v(28.9, 17.78) * mm});
            skLineSegment(sketch, "E138.MirrorCS", {"start": v(3.5, 137.16) * mm, "end": v(3.5, 129.54) * mm});
            skLineSegment(sketch, "E139.MirrorCS", {"start": v(3.5, 81.28) * mm, "end": v(3.5, 73.66) * mm});
            skLineSegment(sketch, "E140.MirrorCS", {"start": v(3.5, 25.4) * mm, "end": v(3.5, 17.78) * mm});
            skLineSegment(sketch, "E141.MirrorCS", {"start": v(54.3, 81.28) * mm, "end": v(54.3, 73.66) * mm});
            skLineSegment(sketch, "E142.MirrorCS", {"start": v(54.3, 25.4) * mm, "end": v(54.3, 17.78) * mm});
            skLineSegment(sketch, "E143.MirrorCS", {"start": v(28.9, 137.16) * mm, "end": v(28.9, 129.54) * mm});
            skLineSegment(sketch, "E144.MirrorCS", {"start": v(28.9, 81.28) * mm, "end": v(28.9, 73.66) * mm});
            skLineSegment(sketch, "E145.MirrorCS", {"start": v(41.91, 86.67) * mm, "end": v(34.3, 86.67) * mm});
            skLineSegment(sketch, "E146.MirrorCS", {"start": v(47.3, 53.34) * mm, "end": v(41.91, 58.73) * mm});
            skLineSegment(sketch, "E147.MirrorCS", {"start": v(16.51, 142.55) * mm, "end": v(8.9, 142.55) * mm});
            skLineSegment(sketch, "E148.MirrorCS", {"start": v(67.3, 86.67) * mm, "end": v(59.7, 86.67) * mm});
            skLineSegment(sketch, "E149.MirrorCS", {"start": v(41.91, 142.55) * mm, "end": v(34.3, 142.55) * mm});
            skLineSegment(sketch, "E150.MirrorCS", {"start": v(47.3, -2.54) * mm, "end": v(41.9, 2.85) * mm});
            skLineSegment(sketch, "E151.MirrorCS", {"start": v(21.9, 109.22) * mm, "end": v(16.51, 114.6) * mm});
            skLineSegment(sketch, "E152.MirrorCS", {"start": v(16.5, 30.79) * mm, "end": v(8.89, 30.79) * mm});
            skLineSegment(sketch, "E153.MirrorCS", {"start": v(41.9, 30.79) * mm, "end": v(34.29, 30.79) * mm});
            skLineSegment(sketch, "E154.MirrorCS", {"start": v(67.3, 30.79) * mm, "end": v(59.69, 30.79) * mm});
            skLineSegment(sketch, "E155.MirrorCS", {"start": v(16.51, 86.67) * mm, "end": v(8.9, 86.67) * mm});
            skLineSegment(sketch, "E156.MirrorCS", {"start": v(59.69, 30.79) * mm, "end": v(54.3, 25.4) * mm});
            skLineSegment(sketch, "E157.MirrorCS", {"start": v(59.7, 86.67) * mm, "end": v(54.3, 81.28) * mm});
            skLineSegment(sketch, "E158.MirrorCS", {"start": v(8.9, 142.55) * mm, "end": v(3.5, 137.16) * mm});
            skLineSegment(sketch, "E159.MirrorCS", {"start": v(34.3, 30.79) * mm, "end": v(28.9, 25.4) * mm});
            skLineSegment(sketch, "E160.MirrorCS", {"start": v(34.3, 86.67) * mm, "end": v(28.9, 81.28) * mm});
            skLineSegment(sketch, "E161.MirrorCS", {"start": v(34.3, 142.55) * mm, "end": v(28.9, 137.16) * mm});
            skLineSegment(sketch, "E162.MirrorCS", {"start": v(8.9, 30.79) * mm, "end": v(3.5, 25.4) * mm});
            skLineSegment(sketch, "E163.MirrorCS", {"start": v(8.9, 86.67) * mm, "end": v(3.5, 81.28) * mm});
            skLineSegment(sketch, "E164.MirrorCS", {"start": v(47.3, 109.22) * mm, "end": v(41.91, 114.6) * mm});
            skPoint(sketch, "E165.MirrorP", {"position": v(57, 126.85) * mm});
            skLineSegment(sketch, "E166.MirrorCS", {"start": v(21.9, 53.34) * mm, "end": v(16.51, 58.73) * mm});
            skLineSegment(sketch, "E167.MirrorCS", {"start": v(72.7, 53.34) * mm, "end": v(67.3, 58.73) * mm});
            skLineSegment(sketch, "E168.MirrorCS", {"start": v(72.7, -2.54) * mm, "end": v(67.3, 2.85) * mm});
            skLineSegment(sketch, "E169.MirrorCS", {"start": v(21.9, 81.28) * mm, "end": v(16.51, 86.67) * mm});
            skLineSegment(sketch, "E170.MirrorCS", {"start": v(21.9, -2.54) * mm, "end": v(16.51, 2.85) * mm});
            skLineSegment(sketch, "E171", {"start": v(72.7, 129.54) * mm, "end": v(72.7, 109.22) * mm, "construction": true});
            skLineSegment(sketch, "E172", {"start": v(72.7, 73.66) * mm, "end": v(72.7, 53.34) * mm, "construction": true});
            skLineSegment(sketch, "E173", {"start": v(72.7, 45.72) * mm, "end": v(72.7, 25.4) * mm, "construction": true});
            skLineSegment(sketch, "E174", {"start": v(72.7, 17.78) * mm, "end": v(72.7, -2.54) * mm, "construction": true});
            skCircle(sketch, "E175", {"center": v(72.7, 63.5) * mm, "radius": 2.03 * mm});
            skCircle(sketch, "E176", {"center": v(72.7, 35.56) * mm, "radius": 2.03 * mm});
            skCircle(sketch, "E177", {"center": v(72.7, 7.62) * mm, "radius": 2.03 * mm});
            skCircle(sketch, "E178", {"center": v(72.7, 119.38) * mm, "radius": 2.03 * mm});
            skLineSegment(sketch, "E179", {"start": v(72.7, 101.6) * mm, "end": v(72.7, 81.28) * mm, "construction": true});
            skCircle(sketch, "E180", {"center": v(72.7, 91.44) * mm, "radius": 2.03 * mm});
            skCircle(sketch, "E181.MirrorC", {"center": v(-72.7, 119.38) * mm, "radius": 2.03 * mm});
            skCircle(sketch, "E182.MirrorC", {"center": v(-72.7, 91.44) * mm, "radius": 2.03 * mm});
            skCircle(sketch, "E183.MirrorC", {"center": v(-72.7, 63.5) * mm, "radius": 2.03 * mm});
            skCircle(sketch, "E184.MirrorC", {"center": v(-72.7, 35.56) * mm, "radius": 2.03 * mm});
            skCircle(sketch, "E185.MirrorC", {"center": v(-72.7, 7.62) * mm, "radius": 2.03 * mm});
            skSolve(sketch);
        }
        {
            var Q0;
            Q0=qSketchRegion(id+"F2",true);
            extrude(context, id + "F3", {"entities" : qUnion([Q0]), "operationType" : NewBodyOperationType.REMOVE, "endBound" : BoundingType.THROUGH_ALL, "oppositeDirection" : true, "depth" : 25.4 * mm, "offsetDistance" : 25.4 * mm});
        }
    });
